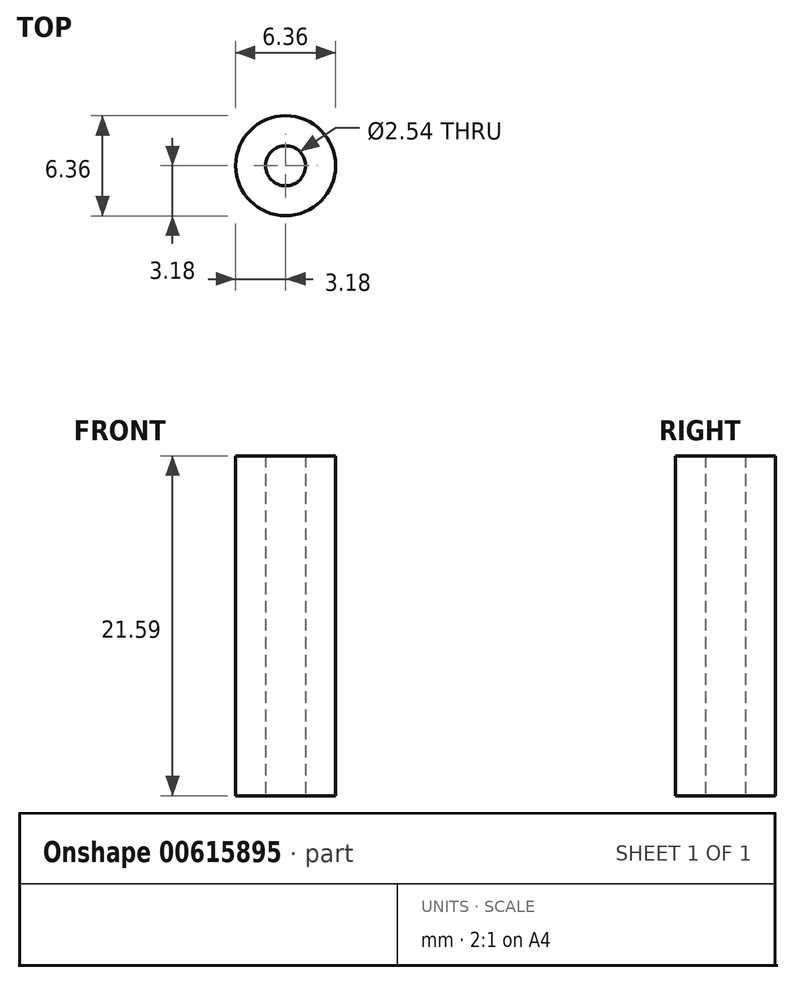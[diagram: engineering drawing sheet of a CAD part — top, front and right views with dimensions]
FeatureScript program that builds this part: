
annotation { "Feature Type Name" : "Feature", "Feature Type Description" : "" }
export const myFeature = defineFeature(function(context is Context, id is Id, definition is map)
    precondition{}
    {
        {
            var Q0;
            Q0=qCreatedBy(makeId("Top.planeOp"),FACE);
            var sketch = newSketch(context, id + "F0", { "sketchPlane" : qUnion([Q0])});
            skCircle(sketch, "E0", {"center": v(0, 0) * mm, "radius": 1.27 * mm});
            skCircle(sketch, "E1", {"center": v(0, 0) * mm, "radius": 3.18 * mm});
            skSolve(sketch);
        }
        {
            var Q0;
            Q0 = qSketchRegion(id + "F0", true);
            extrude(context, id + "F1", {"entities" : qUnion([Q0]), "depth" : 21.59 * mm, "offsetDistance" : 25.4 * mm});
        }
    });
